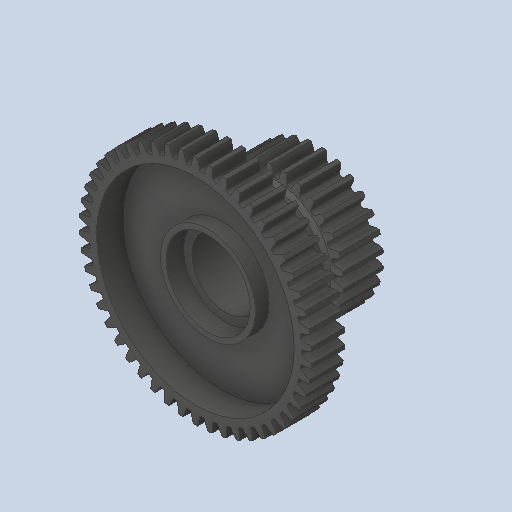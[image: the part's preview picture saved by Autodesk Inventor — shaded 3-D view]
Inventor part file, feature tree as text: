
AUTODESK INVENTOR PART (.ipt)
format: ipt  version: 2023.4 (Build 274418000, 418)  size: 718,336 bytes
history: native  units: in
note: dims shown in document units (in); Inventor stores cm internally (conversion verified against a paired STEP export)
features: chamfer x1
ambient origin geometry x8: Origin, YZ Plane, XZ Plane, XY Plane, X Axis, Y Axis, Z Axis, Center Point
bodies: Solid1 (feature_tree)
feature tree (1):
  chamfer  "Chamfer1"  [1 undecoded]
note: 1 required parameter value undecoded (feature->parameter linkage not recoverable at this tier; creation-order binding heuristic only, values carry confidence <= 0.55)
